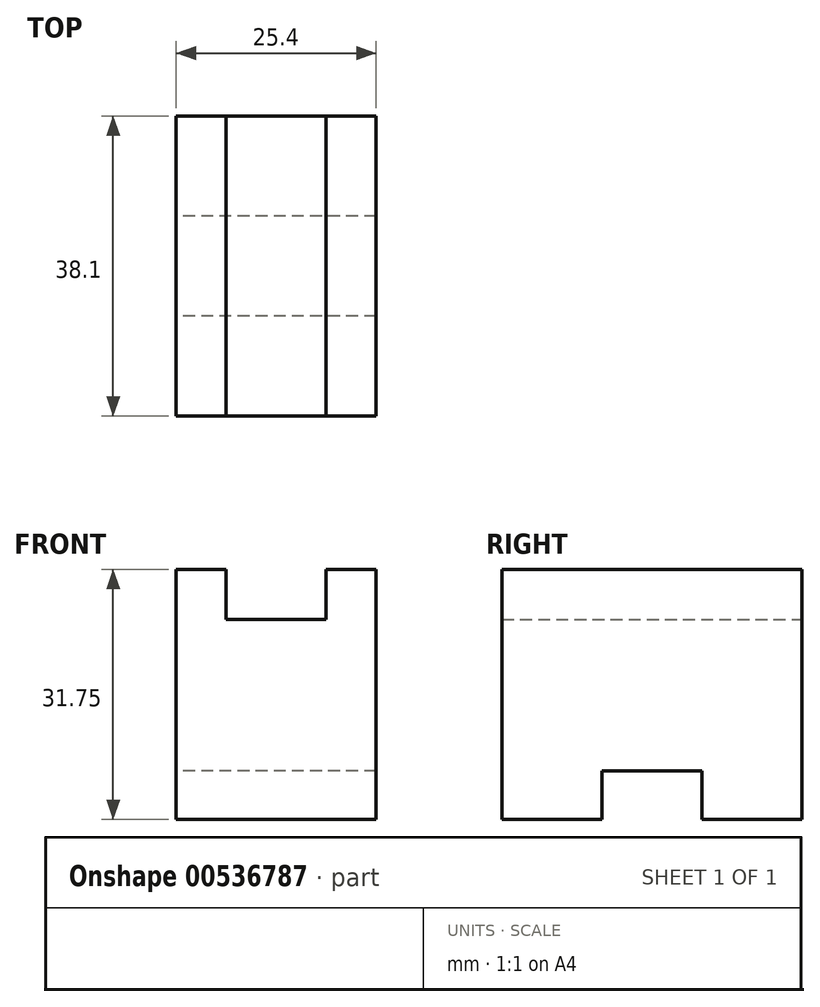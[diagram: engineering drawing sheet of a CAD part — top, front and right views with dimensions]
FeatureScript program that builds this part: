
annotation { "Feature Type Name" : "Feature", "Feature Type Description" : "" }
export const myFeature = defineFeature(function(context is Context, id is Id, definition is map)
    precondition{}
    {
        {
            var Q0;
            Q0=qCreatedBy(makeId("Right.planeOp"),FACE);
            var sketch = newSketch(context, id + "F0", { "sketchPlane" : qUnion([Q0])});
            skLineSegment(sketch, "E0.bottom", {"start": v(-38.61, 50.45) * mm, "end": v(-0.51, 50.45) * mm});
            skLineSegment(sketch, "E0.top", {"start": v(-38.61, 18.7) * mm, "end": v(-0.51, 18.7) * mm});
            skLineSegment(sketch, "E0.left", {"start": v(-38.61, 50.45) * mm, "end": v(-38.61, 18.7) * mm});
            skLineSegment(sketch, "E0.right", {"start": v(-0.51, 50.45) * mm, "end": v(-0.51, 18.7) * mm});
            skSolve(sketch);
        }
        {
            var Q0;
            Q0 = qSketchRegion(id + "F0", true);
            extrude(context, id + "F1", {"entities" : qUnion([Q0]), "depth" : 25.4 * mm, "offsetDistance" : 25.4 * mm});
        }
        {
            var Q0;
            Q0=qCreatedBy(makeId("Front.planeOp"),FACE);
            var sketch = newSketch(context, id + "F2", { "sketchPlane" : qUnion([Q0])});
            skLineSegment(sketch, "E1", {"start": v(19.05, 50.45) * mm, "end": v(19.05, 44.1) * mm});
            skLineSegment(sketch, "E2", {"start": v(19.05, 44.1) * mm, "end": v(6.35, 44.1) * mm});
            skLineSegment(sketch, "E3", {"start": v(6.35, 44.1) * mm, "end": v(6.35, 50.45) * mm});
            skLineSegment(sketch, "E4", {"start": v(6.35, 50.45) * mm, "end": v(19.05, 50.45) * mm});
            skSolve(sketch);
        }
        {
            var Q0;
            Q0 = qSketchRegion(id + "F2", true);
            extrude(context, id + "F3", {"entities" : qUnion([Q0]), "operationType" : NewBodyOperationType.REMOVE, "depth" : 50.8 * mm, "offsetDistance" : 25.4 * mm});
        }
        {
            var Q0;
            Q0=qCreatedBy(makeId("Right.planeOp"),FACE);
            var sketch = newSketch(context, id + "F4", { "sketchPlane" : qUnion([Q0])});
            skLineSegment(sketch, "E5.bottom", {"start": v(-25.91, 24.84) * mm, "end": v(-13.21, 24.84) * mm});
            skLineSegment(sketch, "E5.top", {"start": v(-25.91, 18.5) * mm, "end": v(-13.21, 18.5) * mm});
            skLineSegment(sketch, "E5.left", {"start": v(-25.91, 24.84) * mm, "end": v(-25.91, 18.5) * mm});
            skLineSegment(sketch, "E5.right", {"start": v(-13.21, 24.84) * mm, "end": v(-13.21, 18.5) * mm});
            skSolve(sketch);
        }
        {
            var Q0;
            Q0 = qSketchRegion(id + "F4", true);
            extrude(context, id + "F5", {"entities" : qUnion([Q0]), "operationType" : NewBodyOperationType.REMOVE, "depth" : 25.4 * mm, "offsetDistance" : 25.4 * mm});
        }
        {
            var Q0;
            Q0 = qSketchRegion(id + "F2", true);
            extrude(context, id + "F6", {"entities" : qUnion([Q0]), "operationType" : NewBodyOperationType.REMOVE, "depth" : 50.8 * mm, "offsetDistance" : 25.4 * mm});
        }
        {
            var Q0;
            Q0 = qSketchRegion(id + "F2", true);
            extrude(context, id + "F7", {"entities" : qUnion([Q0]), "operationType" : NewBodyOperationType.REMOVE, "depth" : 50.8 * mm, "offsetDistance" : 25.4 * mm});
        }
    });
